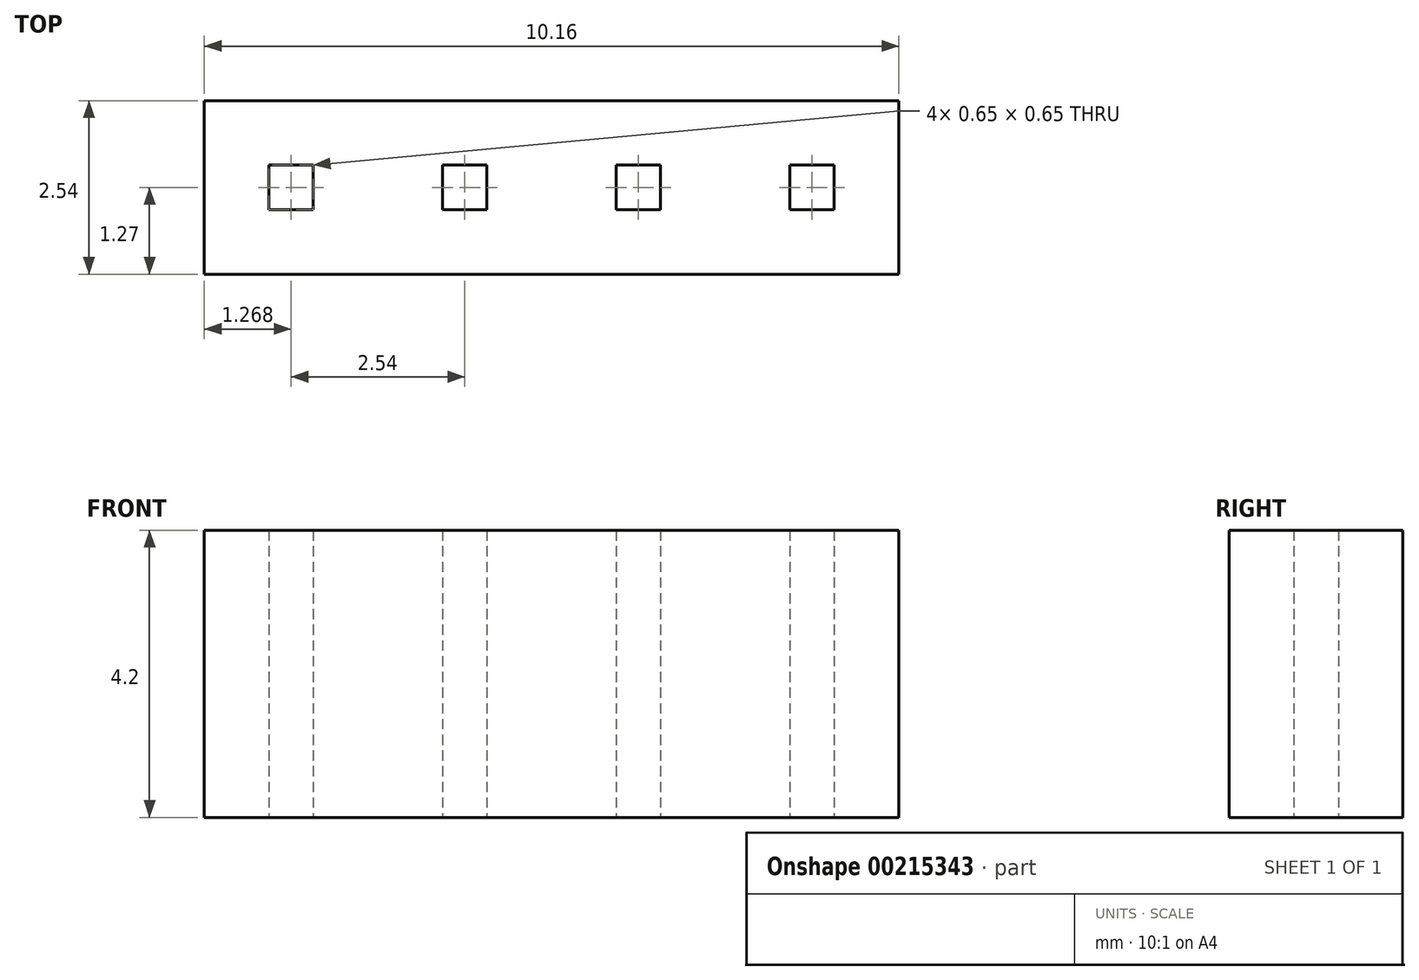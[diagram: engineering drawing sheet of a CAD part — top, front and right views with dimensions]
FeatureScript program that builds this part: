
annotation { "Feature Type Name" : "Feature", "Feature Type Description" : "" }
export const myFeature = defineFeature(function(context is Context, id is Id, definition is map)
    precondition{}
    {
        {
            var Q0;
            Q0=qCreatedBy(makeId("Top.planeOp"),FACE);
            var sketch = newSketch(context, id + "F0", { "sketchPlane" : qUnion([Q0])});
            skLineSegment(sketch, "E0.bottom", {"start": v(-68.73, 0) * mm, "end": v(-71.27, 0) * mm});
            skLineSegment(sketch, "E0.top", {"start": v(-68.73, 2.54) * mm, "end": v(-71.27, 2.54) * mm});
            skLineSegment(sketch, "E0.left", {"start": v(-68.73, 0) * mm, "end": v(-68.73, 2.54) * mm});
            skLineSegment(sketch, "E0.right", {"start": v(-71.27, 0) * mm, "end": v(-71.27, 2.54) * mm});
            skPoint(sketch, "E0.middle", {"position": v(-70, 1.27) * mm});
            skLineSegment(sketch, "E1.left", {"start": v(-68.73, 0.4) * mm, "end": v(-68.73, 1.6) * mm});
            skLineSegment(sketch, "E2.bottom", {"start": v(-70.33, 1.6) * mm, "end": v(-69.68, 1.6) * mm});
            skLineSegment(sketch, "E2.top", {"start": v(-70.33, 0.94) * mm, "end": v(-69.68, 0.94) * mm});
            skLineSegment(sketch, "E2.left", {"start": v(-70.33, 1.6) * mm, "end": v(-70.33, 0.94) * mm});
            skLineSegment(sketch, "E2.right", {"start": v(-69.68, 1.6) * mm, "end": v(-69.68, 0.94) * mm});
            skLineSegment(sketch, "E3.1.0.0", {"start": v(-66.2, 0) * mm, "end": v(-68.73, 0) * mm});
            skLineSegment(sketch, "E3.1.0.1", {"start": v(-66.2, 2.54) * mm, "end": v(-68.73, 2.54) * mm});
            skPoint(sketch, "E3.1.0.2", {"position": v(-67.46, 1.27) * mm});
            skLineSegment(sketch, "E3.1.0.3", {"start": v(-66.2, 0.4) * mm, "end": v(-66.2, 1.6) * mm});
            skPoint(sketch, "E3.1.0.4", {"position": v(-67.46, 1.27) * mm});
            skLineSegment(sketch, "E3.1.0.5", {"start": v(-66.2, 0) * mm, "end": v(-66.2, 2.54) * mm});
            skLineSegment(sketch, "E3.1.0.7", {"start": v(-67.14, 1.6) * mm, "end": v(-67.14, 0.94) * mm});
            skLineSegment(sketch, "E3.1.0.8", {"start": v(-67.79, 1.6) * mm, "end": v(-67.79, 0.94) * mm});
            skLineSegment(sketch, "E3.1.0.9", {"start": v(-67.79, 1.6) * mm, "end": v(-67.14, 1.6) * mm});
            skLineSegment(sketch, "E3.1.0.10", {"start": v(-67.79, 0.94) * mm, "end": v(-67.14, 0.94) * mm});
            skLineSegment(sketch, "E3.2.0.0", {"start": v(-63.65, 0) * mm, "end": v(-66.2, 0) * mm});
            skLineSegment(sketch, "E3.2.0.1", {"start": v(-63.65, 2.54) * mm, "end": v(-66.2, 2.54) * mm});
            skPoint(sketch, "E3.2.0.2", {"position": v(-64.92, 1.27) * mm});
            skLineSegment(sketch, "E3.2.0.3", {"start": v(-63.65, 0.4) * mm, "end": v(-63.65, 1.6) * mm});
            skPoint(sketch, "E3.2.0.4", {"position": v(-64.92, 1.27) * mm});
            skLineSegment(sketch, "E3.2.0.5", {"start": v(-63.65, 0) * mm, "end": v(-63.65, 2.54) * mm});
            skLineSegment(sketch, "E3.2.0.6", {"start": v(-66.2, 0) * mm, "end": v(-66.2, 2.54) * mm});
            skLineSegment(sketch, "E3.2.0.7", {"start": v(-64.6, 1.6) * mm, "end": v(-64.6, 0.94) * mm});
            skLineSegment(sketch, "E3.2.0.8", {"start": v(-65.25, 1.6) * mm, "end": v(-65.25, 0.94) * mm});
            skLineSegment(sketch, "E3.2.0.9", {"start": v(-65.25, 1.6) * mm, "end": v(-64.6, 1.6) * mm});
            skLineSegment(sketch, "E3.2.0.10", {"start": v(-65.25, 0.94) * mm, "end": v(-64.6, 0.94) * mm});
            skLineSegment(sketch, "E3.3.0.0", {"start": v(-61.11, 0) * mm, "end": v(-63.65, 0) * mm});
            skLineSegment(sketch, "E3.3.0.1", {"start": v(-61.11, 2.54) * mm, "end": v(-63.65, 2.54) * mm});
            skPoint(sketch, "E3.3.0.2", {"position": v(-62.38, 1.27) * mm});
            skLineSegment(sketch, "E3.3.0.3", {"start": v(-61.11, 0.4) * mm, "end": v(-61.11, 1.6) * mm});
            skPoint(sketch, "E3.3.0.4", {"position": v(-62.38, 1.27) * mm});
            skLineSegment(sketch, "E3.3.0.5", {"start": v(-61.11, 0) * mm, "end": v(-61.11, 2.54) * mm});
            skLineSegment(sketch, "E3.3.0.6", {"start": v(-63.65, 0) * mm, "end": v(-63.65, 2.54) * mm});
            skLineSegment(sketch, "E3.3.0.7", {"start": v(-62.06, 1.6) * mm, "end": v(-62.06, 0.94) * mm});
            skLineSegment(sketch, "E3.3.0.8", {"start": v(-62.7, 1.6) * mm, "end": v(-62.7, 0.94) * mm});
            skLineSegment(sketch, "E3.3.0.9", {"start": v(-62.7, 1.6) * mm, "end": v(-62.06, 1.6) * mm});
            skLineSegment(sketch, "E3.3.0.10", {"start": v(-62.7, 0.94) * mm, "end": v(-62.06, 0.94) * mm});
            skLineSegment(sketch, "E3.4.0.6", {"start": v(-61.11, 0) * mm, "end": v(-61.11, 2.54) * mm});
            skLineSegment(sketch, "E3.direction1", {"start": v(-71.27, 0) * mm, "end": v(-68.73, 0) * mm, "construction": true});
            skSolve(sketch);
        }
        {
            var Q0;
            Q0=qSketchRegion(id+"F0",true);
            extrude(context, id + "F1", {"entities" : qUnion([Q0]), "depth" : 4.2 * mm});
        }
    });
